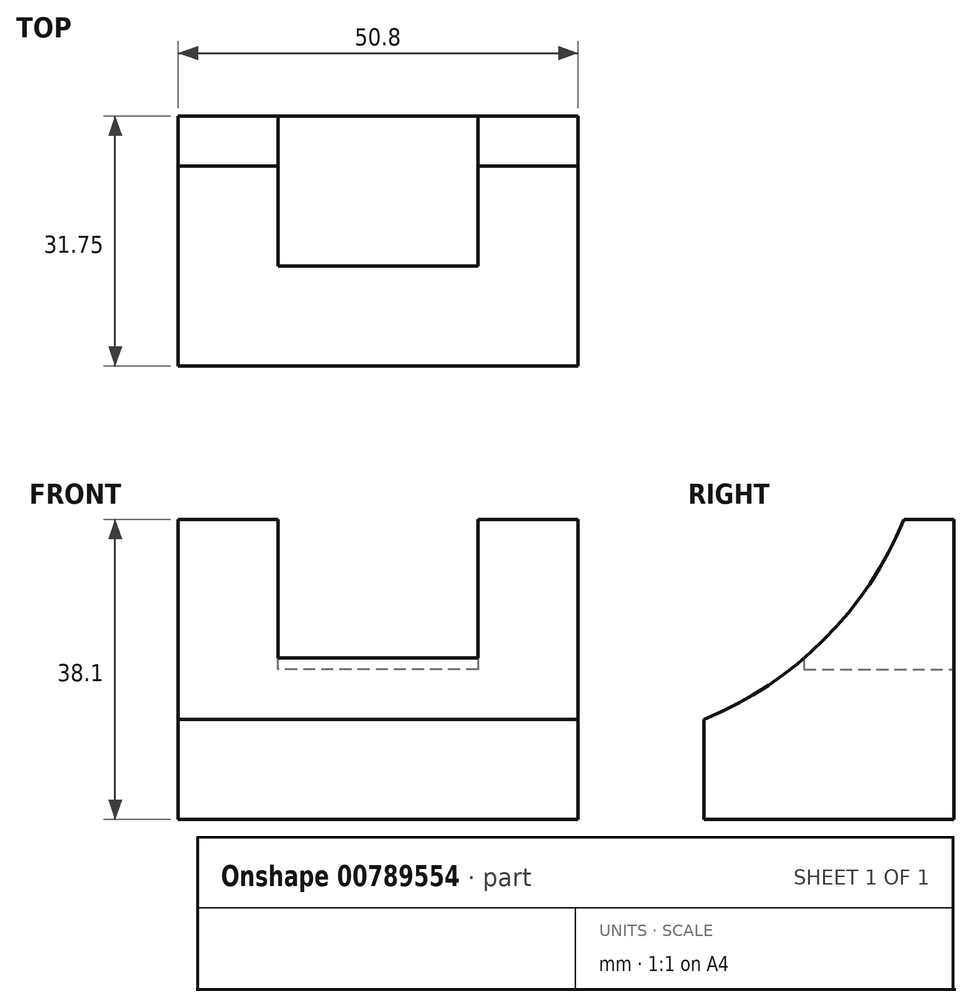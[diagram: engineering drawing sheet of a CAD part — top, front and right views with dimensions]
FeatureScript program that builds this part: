
annotation { "Feature Type Name" : "Feature", "Feature Type Description" : "" }
export const myFeature = defineFeature(function(context is Context, id is Id, definition is map)
    precondition{}
    {
        {
            var Q0;
            Q0=qCreatedBy(makeId("Right.planeOp"),FACE);
            var sketch = newSketch(context, id + "F0", { "sketchPlane" : qUnion([Q0])});
            skLineSegment(sketch, "E0", {"start": v(-26.39, 38.1) * mm, "end": v(-26.39, 0) * mm});
            skLineSegment(sketch, "E1", {"start": v(-26.39, 38.1) * mm, "end": v(5.36, 38.1) * mm});
            skLineSegment(sketch, "E2", {"start": v(5.36, 38.1) * mm, "end": v(5.36, 0) * mm});
            skLineSegment(sketch, "E3", {"start": v(5.36, 0) * mm, "end": v(-26.39, 0) * mm});
            skSolve(sketch);
        }
        {
            var Q0;
            Q0=makeQuery(id+"F0.imprint","IMPRINT",FACE,{"disambiguationData":[TD([[makeQuery(id+"F0.imprint","IMPRINT",EDGE,{"derivedFrom":sQuery(id+"F0.wireOp",EDGE,"E0")}),1.0]])]});
            extrude(context, id + "F1", {"entities" : qUnion([Q0]), "oppositeDirection" : true, "depth" : 50.8 * mm, "offsetDistance" : 25.4 * mm});
        }
        {
            var Q0;
            Q0=makeQuery(id+"F1.opExtrude","CAP_FACE",FACE,{"disambiguationData":[OSD([sQuery(id+"F0.wireOp",EDGE,"E0"),sQuery(id+"F0.wireOp",EDGE,"E1"),sQuery(id+"F0.wireOp",EDGE,"E2"),sQuery(id+"F0.wireOp",EDGE,"E3")])],"isStart":true});
            var sketch = newSketch(context, id + "F2", { "sketchPlane" : qUnion([Q0])});
            skArc(sketch, "E4", {"start": v(-26.39, 12.7) * mm, "mid": v(-11.14, 22.85) * mm, "end": v(-0.99, 38.1) * mm});
            skSolve(sketch);
        }
        {
            var Q0;
            {var subQ0=sQuery(id+"F2.wireOp",EDGE,"E4");Q0=makeQuery(id+"F2.imprint","IMPRINT",FACE,{"disambiguationData":[TD([[makeQuery(id+"F2.imprint","IMPRINT",EDGE,{"derivedFrom":subQ0}),1.0]])]});}
            extrude(context, id + "F3", {"entities" : qUnion([Q0]), "operationType" : NewBodyOperationType.REMOVE, "oppositeDirection" : true, "depth" : 50.8 * mm, "offsetDistance" : 25.4 * mm});
        }
        {
            var Q0;
            Q0=makeQuery(id+"F1.opExtrude","SWEPT_FACE",FACE,{"disambiguationData":[OSD([sQuery(id+"F0.wireOp",EDGE,"E2")])]});
            var sketch = newSketch(context, id + "F4", { "sketchPlane" : qUnion([Q0])});
            skLineSegment(sketch, "E5", {"start": v(12.7, 38.1) * mm, "end": v(12.7, 19.05) * mm});
            skLineSegment(sketch, "E6", {"start": v(12.7, 19.05) * mm, "end": v(38.1, 19.05) * mm});
            skLineSegment(sketch, "E7", {"start": v(38.1, 19.05) * mm, "end": v(38.1, 38.1) * mm});
            skSolve(sketch);
        }
        {
            var Q0;
            {var subQ0=sQuery(id+"F4.wireOp",EDGE,"E5");Q0=makeQuery(id+"F4.imprint","IMPRINT",FACE,{"disambiguationData":[TD([[makeQuery(id+"F4.imprint","IMPRINT",EDGE,{"derivedFrom":subQ0}),1.0]])]});}
            extrude(context, id + "F5", {"entities" : qUnion([Q0]), "operationType" : NewBodyOperationType.REMOVE, "oppositeDirection" : true, "depth" : 19.05 * mm});
        }
    });
